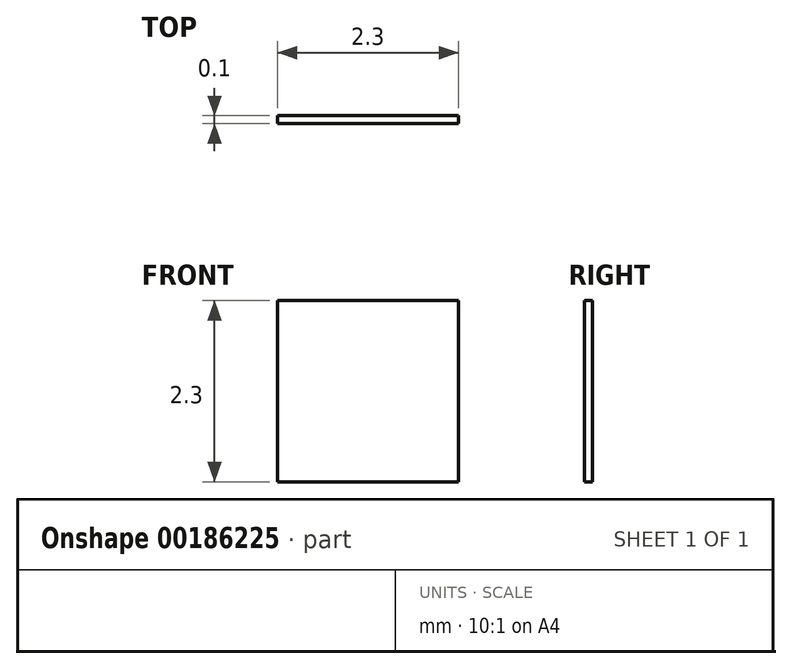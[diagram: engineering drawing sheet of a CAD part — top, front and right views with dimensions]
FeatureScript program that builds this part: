
annotation { "Feature Type Name" : "Feature", "Feature Type Description" : "" }
export const myFeature = defineFeature(function(context is Context, id is Id, definition is map)
    precondition{}
    {
        {
            var Q0;
            Q0=qCreatedBy(makeId("Front.planeOp"),FACE);
            var sketch = newSketch(context, id + "F0", { "sketchPlane" : qUnion([Q0])});
            skLineSegment(sketch, "E0.bottom", {"start": v(1.15, 1.15) * mm, "end": v(-1.15, 1.15) * mm});
            skLineSegment(sketch, "E0.top", {"start": v(1.15, -1.15) * mm, "end": v(-1.15, -1.15) * mm});
            skLineSegment(sketch, "E0.left", {"start": v(1.15, 1.15) * mm, "end": v(1.15, -1.15) * mm});
            skLineSegment(sketch, "E0.right", {"start": v(-1.15, 1.15) * mm, "end": v(-1.15, -1.15) * mm});
            skPoint(sketch, "E0.middle", {"position": v(0, 0) * mm});
            skSolve(sketch);
        }
        {
            var Q0;
            Q0=makeQuery(id+"F0.imprint","IMPRINT",FACE,{"disambiguationData":[TD([[makeQuery(id+"F0.imprint","IMPRINT",EDGE,{"derivedFrom":sQuery(id+"F0.wireOp",EDGE,"E0.bottom")}),1.0]])]});
            extrude(context, id + "F1", {"entities" : qUnion([Q0]), "depth" : 0.1 * mm});
        }
    });
